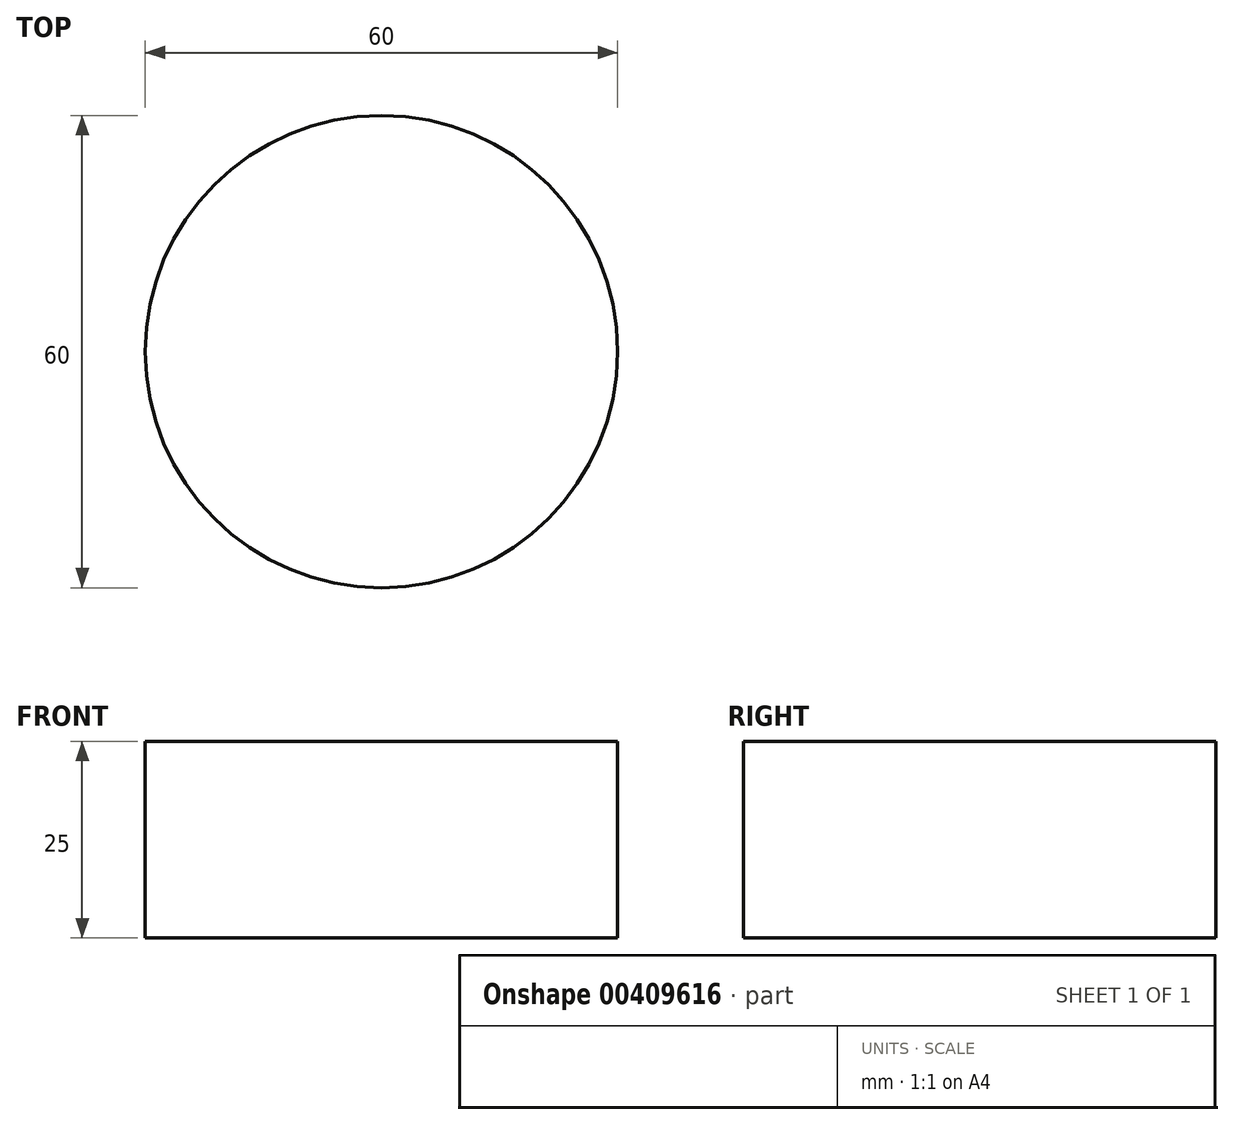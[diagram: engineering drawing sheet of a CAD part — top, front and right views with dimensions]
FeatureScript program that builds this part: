
annotation { "Feature Type Name" : "Feature", "Feature Type Description" : "" }
export const myFeature = defineFeature(function(context is Context, id is Id, definition is map)
    precondition{}
    {
        {
            var Q0;
            Q0=qCreatedBy(makeId("Top.planeOp"),FACE);
            var sketch = newSketch(context, id + "F0", { "sketchPlane" : qUnion([Q0])});
            skCircle(sketch, "E0", {"center": v(0, 0) * mm, "radius": 30 * mm});
            skSolve(sketch);
        }
        {
            var Q0;
            Q0=makeQuery(id+"F0.imprint","IMPRINT",FACE,{"disambiguationData":[TD([[makeQuery(id+"F0.imprint","IMPRINT",EDGE,{"derivedFrom":sQuery(id+"F0.wireOp",EDGE,"E0")}),1.0]])]});
            var Q1;
            Q1=sQuery(id+"F0.wireOp",EDGE,"E0");
            extrude(context, id + "F1", {"entities" : qUnion([Q0]), "bodyType" : ToolBodyType.SURFACE, "surfaceEntities" : qUnion([Q1]), "depth" : 25 * mm, "offsetDistance" : 25 * mm});
        }
    });
